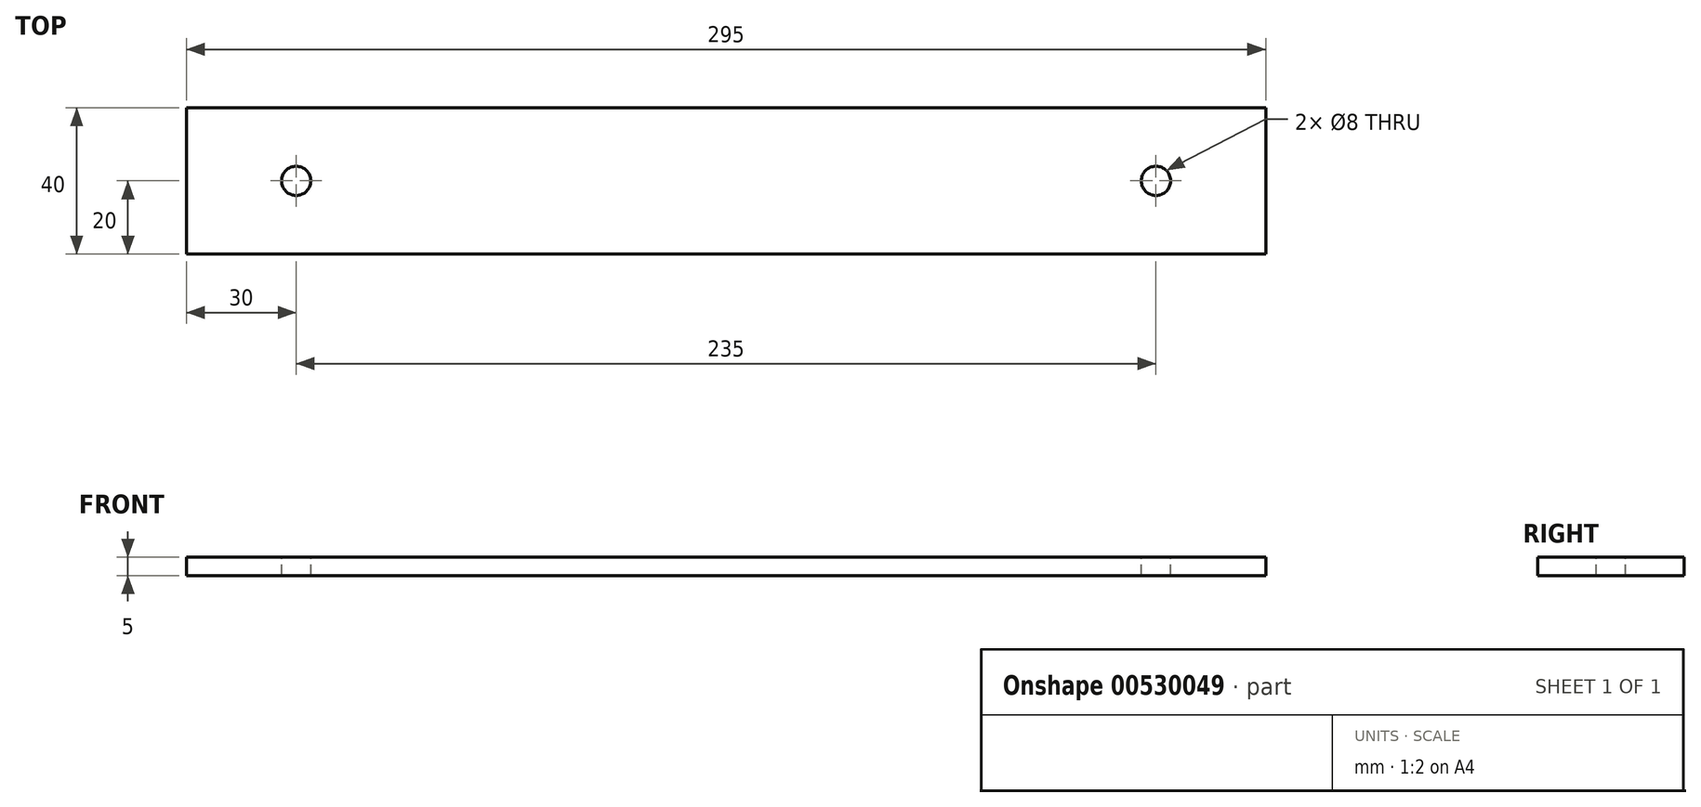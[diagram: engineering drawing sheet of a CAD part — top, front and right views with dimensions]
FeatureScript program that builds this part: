
annotation { "Feature Type Name" : "Feature", "Feature Type Description" : "" }
export const myFeature = defineFeature(function(context is Context, id is Id, definition is map)
    precondition{}
    {
        {
            var Q0;
            Q0=qCreatedBy(makeId("Top.planeOp"),FACE);
            var sketch = newSketch(context, id + "F0", { "sketchPlane" : qUnion([Q0])});
            skLineSegment(sketch, "E0.bottom", {"start": v(147.5, -20) * mm, "end": v(-147.5, -20) * mm});
            skLineSegment(sketch, "E0.top", {"start": v(147.5, 20) * mm, "end": v(-147.5, 20) * mm});
            skLineSegment(sketch, "E0.left", {"start": v(147.5, -20) * mm, "end": v(147.5, 20) * mm});
            skLineSegment(sketch, "E0.right", {"start": v(-147.5, -20) * mm, "end": v(-147.5, 20) * mm});
            skPoint(sketch, "E0.middle", {"position": v(0, 0) * mm});
            skSolve(sketch);
        }
        {
            var Q0;
            Q0=makeQuery(id+"F0.imprint","IMPRINT",FACE,{"disambiguationData":[TD([[makeQuery(id+"F0.imprint","IMPRINT",EDGE,{"derivedFrom":sQuery(id+"F0.wireOp",EDGE,"E0.bottom")}),-1.0]])]});
            extrude(context, id + "F1", {"entities" : qUnion([Q0]), "depth" : 5 * mm, "offsetDistance" : 25 * mm});
        }
        {
            var Q0;
            Q0=makeQuery(id+"F1.opExtrude","CAP_FACE",FACE,{"disambiguationData":[OSD([sQuery(id+"F0.wireOp",EDGE,"E0.bottom"),sQuery(id+"F0.wireOp",EDGE,"E0.top"),sQuery(id+"F0.wireOp",EDGE,"E0.left"),sQuery(id+"F0.wireOp",EDGE,"E0.right")])],"isStart":false});
            var sketch = newSketch(context, id + "F2", { "sketchPlane" : qUnion([Q0])});
            skCircle(sketch, "E1", {"center": v(-117.5, 0) * mm, "radius": 4 * mm});
            skCircle(sketch, "E2", {"center": v(117.5, 0) * mm, "radius": 4 * mm});
            skSolve(sketch);
        }
        {
            var Q0;
            Q0 = qSketchRegion(id + "F2", true);
            extrude(context, id + "F3", {"entities" : qUnion([Q0]), "operationType" : NewBodyOperationType.REMOVE, "oppositeDirection" : true, "depth" : 25 * mm, "offsetDistance" : 25 * mm});
        }
    });
